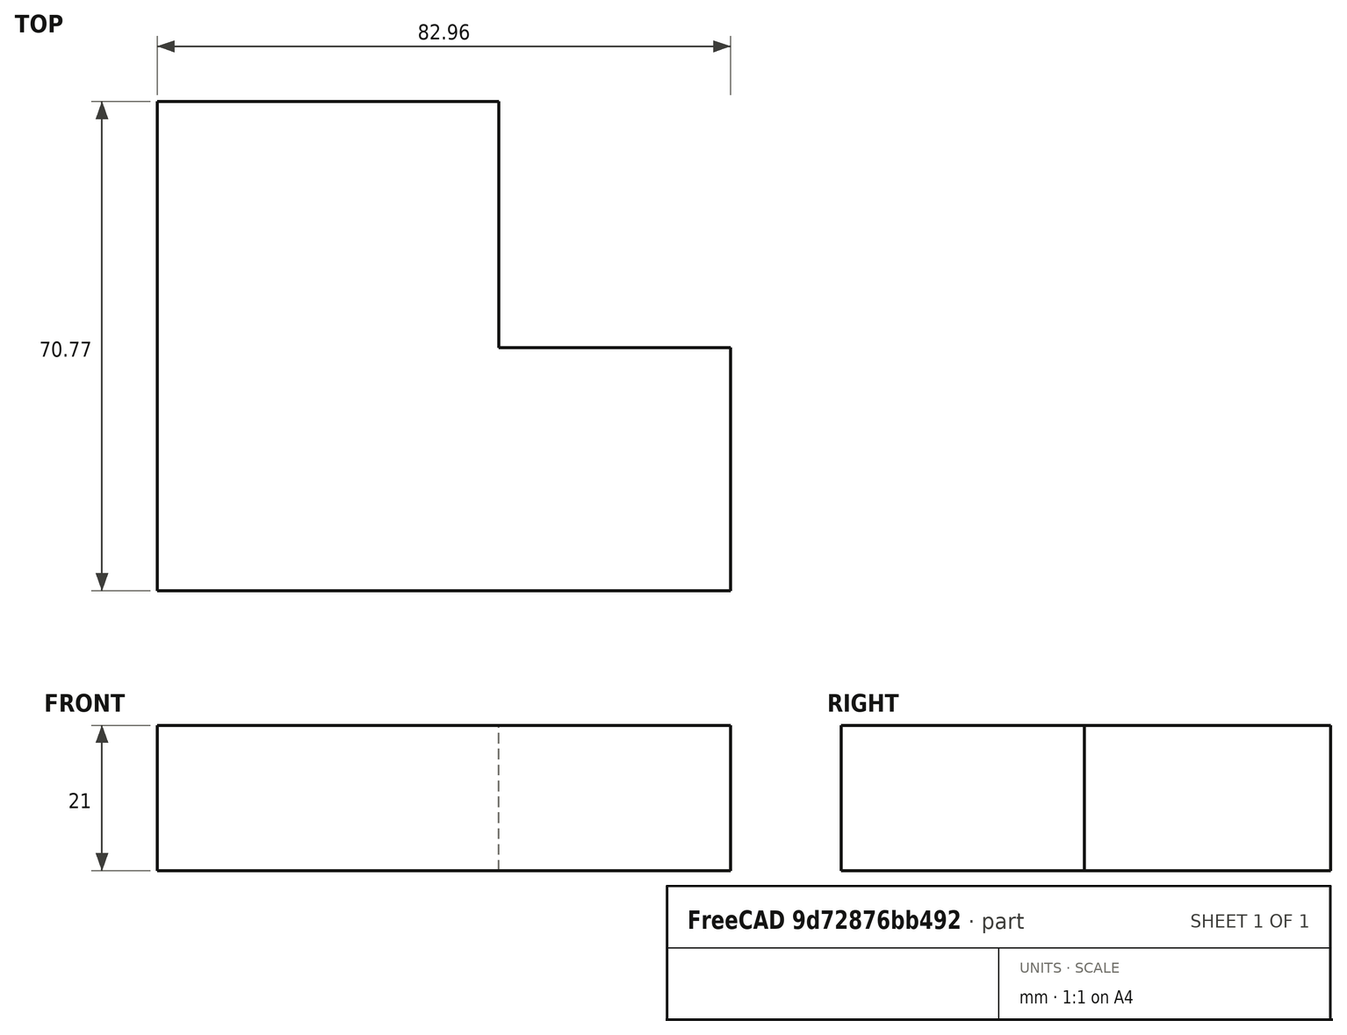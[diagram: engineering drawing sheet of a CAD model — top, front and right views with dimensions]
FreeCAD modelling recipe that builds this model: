
FCSTD DOCUMENT  (FreeCAD 0.20R29603 (Git))
Label: Simple_Try_FEM
License: All rights reserved
LicenseURL: http://en.wikipedia.org/wiki/All_rights_reserved
objects: Fem::FemSolverObjectPython×3, PartDesign::Body×2, Sketcher::SketchObject×1, PartDesign::Pad×1, App::MaterialObjectPython×1, Fem::FemMeshObjectPython×1, Fem::ConstraintFixed×1, Fem::ConstraintSpring×1, Fem::FemAnalysis×1
note: 5 computed .brp shape members not serialized (recipe doc carries the construction recipe); baked Part::Feature solids carry a one-line shape summary decoded from their .brp

FEATURE [Sketcher::SketchObject] Sketch
  FullyConstrained = false
  MapMode = 5
  Support = -> [XY_Plane001]
  sketch-geometry (6):
    g0: LineSegment StartX=-38.0064 StartY=35.6295 StartZ=0 EndX=11.4006 EndY=35.6295 EndZ=0
    g1: LineSegment StartX=44.946 StartY=0 StartZ=0 EndX=44.946 EndY=-35.1428 EndZ=0
    g2: LineSegment StartX=44.946 StartY=-35.1428 StartZ=0 EndX=-38.0064 EndY=-35.1428 EndZ=0
    g3: LineSegment StartX=-38.0064 StartY=-35.1428 StartZ=0 EndX=-38.0064 EndY=35.6295 EndZ=0
    g4: LineSegment StartX=11.4006 StartY=35.6295 StartZ=0 EndX=11.4006 EndY=0 EndZ=0
    g5: LineSegment StartX=11.4006 StartY=0 StartZ=0 EndX=44.946 EndY=0 EndZ=0
  constraints (13):
    c: Coincident(g1,g2)
    c: Coincident(g2,g3)
    c: Coincident(g3,g0)
    c: Horizontal(g0)
    c: Horizontal(g2)
    c: Vertical(g1)
    c: Vertical(g3)
    c: PointOnObject(g4,g-1)
    c: Vertical(g4)
    c: Coincident(g5,g4)
    c: Horizontal(g5)
    c: Coincident(g0,g4)
    c: Coincident(g1,g5)
FEATURE [PartDesign::Body] Body
  Origin = -> Origin
FEATURE [PartDesign::Pad] Pad
  Direction = (0,0,1)
  Length = 21
  Length2 = 10
  Profile = -> Sketch
  ReferenceAxis = -> Sketch [N_Axis]
  Type = 0
FEATURE [PartDesign::Body] Body001
  Group = -> [Sketch,Pad]
  Origin = -> Origin001
  Tip = -> Pad
FEATURE [Fem::FemSolverObjectPython] SolverCcxTools  # FEM object (typed FeaturePython)
  AnalysisType = 0
  BeamShellResultOutput3D = false
  BucklingFactors = 1
  EigenmodeHighLimit = 1000000
  EigenmodeLowLimit = 0
  EigenmodesCount = 10
  GeometricalNonlinearity = 0
  IterationsControlParameterCutb = 0.25,0.5,0.75,0.85,,,1.5,
  IterationsControlParameterIter = 4,8,9,200,10,400,,200,,
  IterationsControlParameterTimeUse = false
  IterationsThermoMechMaximum = 200
  IterationsUserDefinedIncrementations = false
  IterationsUserDefinedTimeStepLength = false
  MaterialNonlinearity = 0
  MatrixSolverType = 0
  SplitInputWriter = false
  ThermoMechSteadyState = false
  TimeEnd = 1
  TimeInitialStep = 1
FEATURE [App::MaterialObjectPython] MaterialSolid  # material (typed FeaturePython)
  Category = 0
FEATURE [Fem::FemMeshObjectPython] FEMMeshGmsh  # FEM object (typed FeaturePython)
  Algorithm2D = 0
  Algorithm3D = 0
  CharacteristicLengthMax = 0
  CharacteristicLengthMin = 0
  CoherenceMesh = true
  ElementDimension = 0
  ElementOrder = 1
  GeometryTolerance = 1e-06
  GroupsOfNodes = false
  HighOrderOptimize = 0
  MeshSizeFromCurvature = 12
  OptimizeNetgen = false
  OptimizeStd = true
  Part = -> Pad
  RecombinationAlgorithm = 0
  Recombine3DAll = false
  RecombineAll = false
  SecondOrderLinear = false
FEATURE [Fem::ConstraintFixed] ConstraintFixed
  NormalDirection = (0,-1,0)
  Normals = (24) [(0,-1,0),(0,-1,0),(0,-1,0),(0,-1,0),(0,-1,0),(0,-1,0),(0,-1,0),(0,-1,0),(0,-1,0),(0,-1,0),(0,-1,0),(0,-1,0),(0,0,1),(0,0,1),(0,0,1),(0,0,1),(0,0,1),+7 more]
  Points = (24) [(44.946,-35.1428,21),(17.2952,-35.1428,21),(-10.3556,-35.1428,21),(-38.0064,-35.1428,21),(44.946,-35.1428,10.5),(17.2952,-35.1428,10.5),+18 more]
  References = -> [Pad]
  Scale = 8
FEATURE [Fem::ConstraintSpring] ConstraintSpring
  NormalDirection = (0,0,1)
  Normals = (12) [(0,0,1),(0,0,1),(0,0,1),(0,0,1),(0,0,1),(0,0,1),(0,0,1),(0,0,1),(0,0,1),(0,0,1),(0,0,1),(0,0,1)]
  Points = (12) [(-38.0064,-35.1428,21),(-10.3556,-35.1428,21),(17.2952,-35.1428,21),(44.946,-35.1428,21),(-38.0064,-11.552,21),(-10.3556,-11.552,21),+6 more]
  References = -> [Pad]
  Scale = 8
  normalStiffness = 1
  tangentialStiffness = 0
FEATURE [Fem::FemSolverObjectPython] SolverElmer  # FEM object (typed FeaturePython)
  BDFOrder = 2
  SimulationType = 1
  SteadyStateMaxIterations = 1
  SteadyStateMinIterations = 0
  TimestepIntervals = [100]
  TimestepSizes = [0.1]
FEATURE [Fem::FemSolverObjectPython] SolverZ88  # FEM object (typed FeaturePython)
  AnalysisType = 0
FEATURE [Fem::FemAnalysis] Analysis
  Group = -> [SolverCcxTools,MaterialSolid,FEMMeshGmsh,ConstraintFixed,ConstraintSpring,SolverElmer,SolverZ88]
